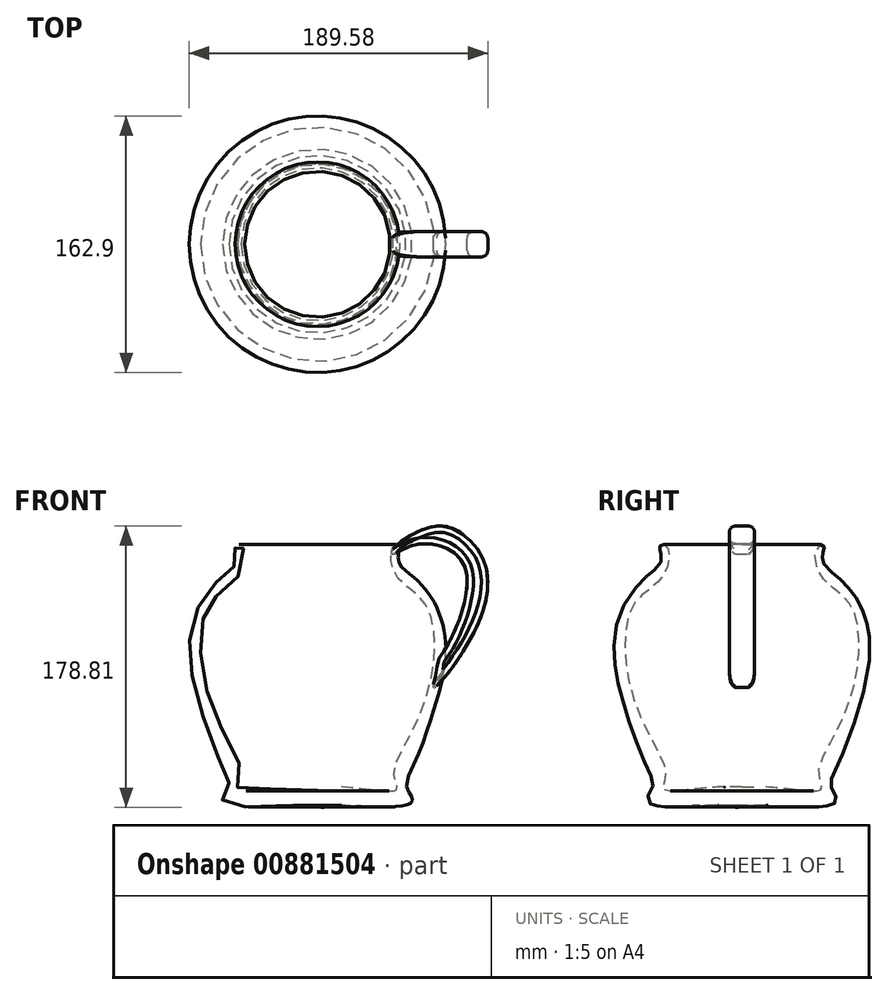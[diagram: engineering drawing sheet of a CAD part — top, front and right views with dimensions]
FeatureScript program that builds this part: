
annotation { "Feature Type Name" : "Feature", "Feature Type Description" : "" }
export const myFeature = defineFeature(function(context is Context, id is Id, definition is map)
    precondition{}
    {
        {
            var Q0;
            Q0=qCreatedBy(makeId("Front.planeOp"),FACE);
            var sketch = newSketch(context, id + "F0", { "sketchPlane" : qUnion([Q0])});
            skLineSegment(sketch, "E0", {"start": v(72.87, -52) * mm, "end": v(72.87, 114.1) * mm});
            skFitSpline(sketch, "E1", {"points": [v(72.87, -41.87) * mm, v(23.03, -41.89) * mm, v(24.23, -33.66) * mm, v(13.21, -5.45) * mm, v(0, 32.66) * mm, v(0, 65.6) * mm, v(8.1, 80.86) * mm, v(24.2, 96.72) * mm, v(24.68, 113.58) * mm, v(20.98, 113.37) * mm, v(20.58, 112.25) * mm, v(21.5, 103.53) * mm, v(13.96, 95.03) * mm, v(0, 79.53) * mm, v(-8.41, 52.49) * mm, v(-3.58, 17.73) * mm, v(11.8, -25.69) * mm, v(16.4, -39.56) * mm, v(12.54, -47.84) * mm, v(19.56, -52) * mm, v(64.81, -52) * mm, v(72.87, -52) * mm, v(72.87, -41.87) * mm]});
            skSolve(sketch);
        }
        {
            var Q0;
            {var subQ0=sQuery(id+"F0.wireOp",EDGE,"E1");var subQ1=sQuery(id+"F0.wireOp",EDGE,"E0");var subQ2=makeQuery(id+"F0.imprint","INTERSECT",VERTEX,{"disambiguationData":[OD(0.0)],"derivedFrom":[subQ1,subQ0]});Q0=makeQuery(id+"F0.imprint","IMPRINT",FACE,{"disambiguationData":[TD([[makeQuery(id+"F0.imprint","IMPRINT",EDGE,{"disambiguationData":[TD([[subQ2,-1.0]])],"derivedFrom":subQ1}),1.0]])]});}
            var Q1;
            Q1=sQuery(id+"F0.wireOp",EDGE,"E0");
            revolve(context, id + "F1", {"surfaceOperationType" : NewSurfaceOperationType.NEW, "entities" : qUnion([Q0]), "axis" : qUnion([Q1]), "revolveType" : RevolveType.FULL});
        }
        {
            var Q0;
            Q0=qCreatedBy(makeId("Front.planeOp"),FACE);
            var sketch = newSketch(context, id + "F2", { "sketchPlane" : qUnion([Q0])});
            skFitSpline(sketch, "E2", {"points": [v(146.67, 23.35) * mm, v(173.18, 60.2) * mm, v(179.73, 100.41) * mm, v(169.09, 117.35) * mm, v(147.65, 125.7) * mm, v(120.12, 110.32) * mm, v(120.38, 108.05) * mm, v(133.1, 113.44) * mm, v(157.37, 110.5) * mm, v(167.96, 90.67) * mm, v(155.04, 49.44) * mm, v(149.17, 40.24) * mm, v(148.2, 32.44) * mm, v(146.67, 23.35) * mm]});
            skSolve(sketch);
        }
        {
            var Q0;
            Q0 = qSketchRegion(id + "F2", true);
            extrude(context, id + "F3", {"entities" : qUnion([Q0]), "depth" : 8 * mm, "offsetDistance" : 25.4 * mm, "hasSecondDirection" : true, "secondDirectionOppositeDirection" : true, "secondDirectionDepth" : 8 * mm});
        }
        {
            var Q0;
            Q0=makeQuery(id+"F3.opExtrude","SWEPT_FACE",FACE,{"disambiguationData":[OSD([sQuery(id+"F2.wireOp",EDGE,"E2")])]});
            fillet(context, id + "F4", {"entities" : qUnion([Q0]), "radius" : 4 * mm, "tangentPropagation" : true, "allowEdgeOverflow" : false});
        }
    });
